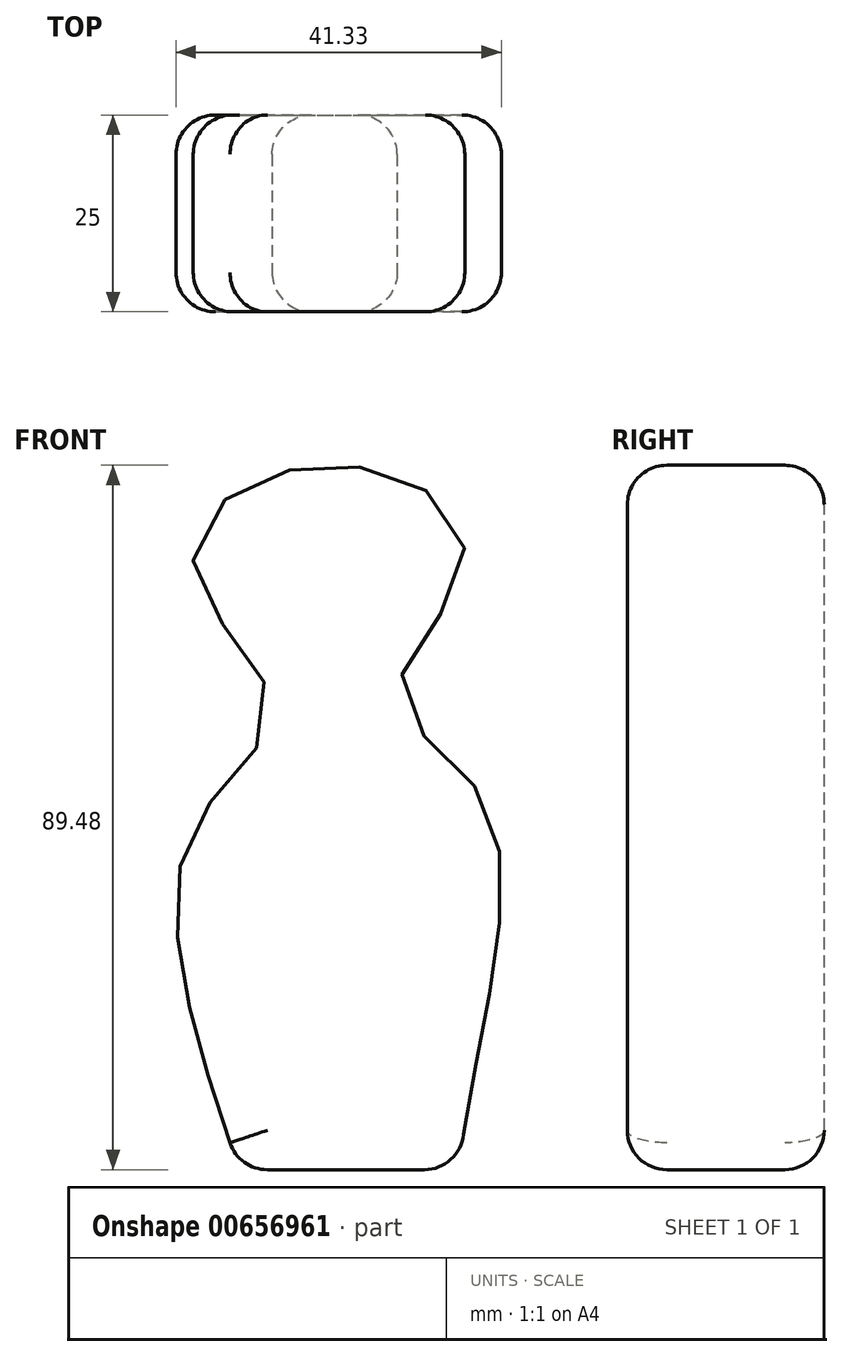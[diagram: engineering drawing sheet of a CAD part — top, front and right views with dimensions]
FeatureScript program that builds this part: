
annotation { "Feature Type Name" : "Feature", "Feature Type Description" : "" }
export const myFeature = defineFeature(function(context is Context, id is Id, definition is map)
    precondition{}
    {
        {
            var Q0;
            Q0=qCreatedBy(makeId("Front.planeOp"),FACE);
            var sketch = newSketch(context, id + "F0", { "sketchPlane" : qUnion([Q0])});
            skLineSegment(sketch, "E0", {"start": v(-13.95, -38.1) * mm, "end": v(14.85, -38.1) * mm});
            skFitSpline(sketch, "E1", {"points": [v(-13.95, -38.1) * mm, v(-20.25, 4.2) * mm, v(-9.75, 20.4) * mm, v(-19.35, 36.9) * mm, v(-13.95, 48.3) * mm, v(6.75, 49.8) * mm, v(14.55, 38.4) * mm, v(6.15, 21.9) * mm, v(18.45, 5.7) * mm, v(14.85, -38.1) * mm, v(47.25, -9) * mm], "startDerivative": vector(-122.36, 361.77) * mm, "endDerivative": vector(334.21, 376.48) * mm});
            skSolve(sketch);
        }
        {
            var Q0;
            Q0 = qSketchRegion(id + "F0", true);
            extrude(context, id + "F1", {"entities" : qUnion([Q0]), "depth" : 25 * mm, "offsetDistance" : 25 * mm});
        }
        {
            var Q0;
            Q0=makeQuery(id+"F1.opExtrude","CAP_EDGE",EDGE,{"disambiguationData":[OSD([sQuery(id+"F0.wireOp",EDGE,"E1")])],"isStart":false});
            var Q1;
            Q1=makeQuery(id+"F1.opExtrude","CAP_EDGE",EDGE,{"disambiguationData":[OSD([sQuery(id+"F0.wireOp",EDGE,"E1")])],"isStart":true});
            var Q2;
            Q2=makeQuery(id+"F1.opExtrude","SWEPT_FACE",FACE,{"disambiguationData":[OSD([sQuery(id+"F0.wireOp",EDGE,"E1")])]});
            fillet(context, id + "F2", {"entities" : qUnion([Q0, Q1, Q2]), "radius" : 5 * mm, "tangentPropagation" : true, "allowEdgeOverflow" : false});
        }
        {
            var Q0;
            {var subQ0=sQuery(id+"F0.wireOp",EDGE,"E0");var subQ1=sQuery(id+"F0.wireOp",EDGE,"E1");Q0=makeQuery(id+"F2.opFillet","BLEND_EDGE",EDGE,{"blendedFrom":[makeQuery(id+"F1.opExtrude","SWEPT_EDGE",EDGE,{"disambiguationData":[OSD([subQ0,subQ1]),TDD([makeQuery(id+"F0.imprint","INTERSECT",VERTEX,{"disambiguationData":[OD(0.0)],"derivedFrom":[subQ0,subQ1]})])]}),makeQuery(id+"F1.opExtrude","SWEPT_FACE",FACE,{"disambiguationData":[OSD([subQ0])]})],"blendedInto":[makeQuery(id+"F1.opExtrude","SWEPT_FACE",FACE,{"disambiguationData":[OSD([subQ0])]})]});}
            var Q1;
            {var subQ0=sQuery(id+"F0.wireOp",EDGE,"E1");var subQ1=sQuery(id+"F0.wireOp",EDGE,"E0");Q1=makeQuery(id+"F2.opFillet","BLEND_EDGE",EDGE,{"blendedFrom":[makeQuery(id+"F1.opExtrude","SWEPT_EDGE",EDGE,{"disambiguationData":[OSD([subQ1,subQ0]),TDD([makeQuery(id+"F0.imprint","INTERSECT",VERTEX,{"disambiguationData":[OD(0.0)],"derivedFrom":[subQ1,subQ0]})])]}),makeQuery(id+"F1.opExtrude","SWEPT_FACE",FACE,{"disambiguationData":[OSD([subQ0])]})],"blendedInto":[makeQuery(id+"F1.opExtrude","SWEPT_FACE",FACE,{"disambiguationData":[OSD([subQ0])]})]});}
            var Q2;
            Q2=makeQuery(id+"F1.opExtrude","CAP_EDGE",EDGE,{"disambiguationData":[OSD([sQuery(id+"F0.wireOp",EDGE,"E0")])],"isStart":false});
            var Q3;
            Q3=makeQuery(id+"F1.opExtrude","SWEPT_FACE",FACE,{"disambiguationData":[OSD([sQuery(id+"F0.wireOp",EDGE,"E0")])]});
            var Q4;
            {var subQ0=sQuery(id+"F0.wireOp",EDGE,"E1");var subQ1=sQuery(id+"F0.wireOp",EDGE,"E0");Q4=makeQuery(id+"F2.opFillet","BLEND_FACE",FACE,{"disambiguationData":[OSD([subQ1,subQ0]),TDD([makeQuery(id+"F1.opExtrude","SWEPT_EDGE",EDGE,{"disambiguationData":[OSD([subQ1,subQ0]),TDD([makeQuery(id+"F0.imprint","INTERSECT",VERTEX,{"disambiguationData":[OD(1.0)],"derivedFrom":[subQ1,subQ0]})])]})])]});}
            var Q5;
            {var subQ0=sQuery(id+"F0.wireOp",EDGE,"E1");var subQ1=sQuery(id+"F0.wireOp",EDGE,"E0");Q5=makeQuery(id+"F2.opFillet","BLEND_FACE",FACE,{"disambiguationData":[OSD([subQ1,subQ0]),TDD([makeQuery(id+"F1.opExtrude","SWEPT_EDGE",EDGE,{"disambiguationData":[OSD([subQ1,subQ0]),TDD([makeQuery(id+"F0.imprint","INTERSECT",VERTEX,{"disambiguationData":[OD(0.0)],"derivedFrom":[subQ1,subQ0]})])]})])]});}
            fillet(context, id + "F3", {"entities" : qUnion([Q0, Q1, Q2, Q3, Q4, Q5]), "radius" : 5 * mm, "tangentPropagation" : true, "allowEdgeOverflow" : false});
        }
    });
